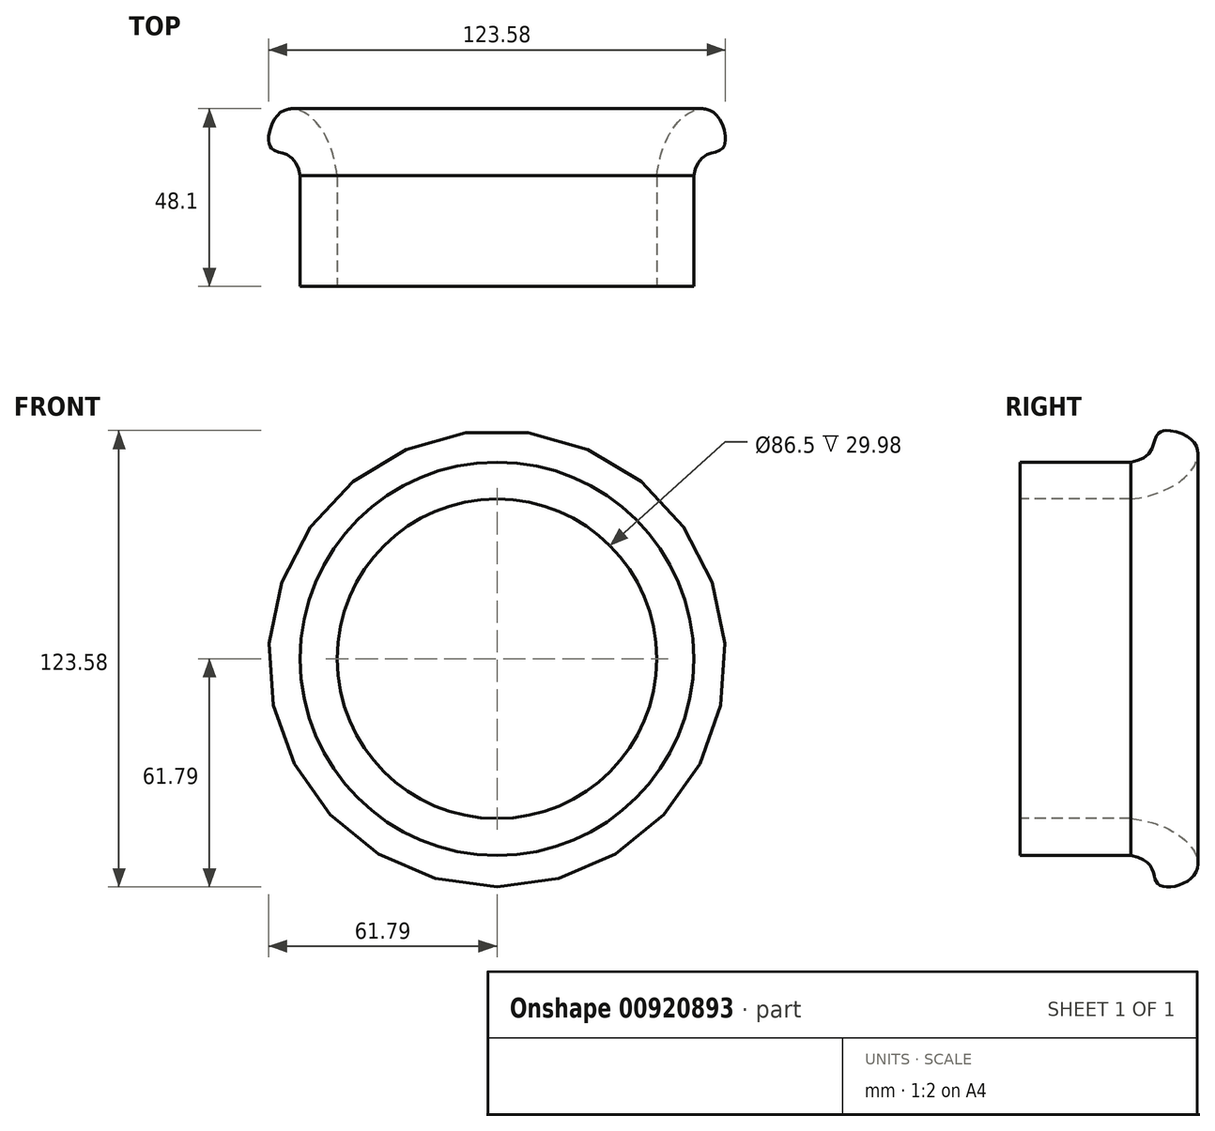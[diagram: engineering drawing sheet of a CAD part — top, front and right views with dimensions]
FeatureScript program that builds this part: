
annotation { "Feature Type Name" : "Feature", "Feature Type Description" : "" }
export const myFeature = defineFeature(function(context is Context, id is Id, definition is map)
    precondition{}
    {
        {
            var Q0;
            Q0=qCreatedBy(makeId("Right.planeOp"),FACE);
            var sketch = newSketch(context, id + "F0", { "sketchPlane" : qUnion([Q0])});
            skLineSegment(sketch, "E0.0", {"start": v(-12.36, -53.25) * mm, "end": v(17.64, -53.25) * mm});
            skFitSpline(sketch, "E1", {"points": [v(17.62, -43.25) * mm, v(35.05, -58.14) * mm, v(25.1, -61.1) * mm, v(17.64, -53.25) * mm], "startDerivative": vector(100.58, -11.6) * mm, "endDerivative": vector(-76.73, 13.48) * mm});
            skLineSegment(sketch, "E2", {"start": v(-12.36, -53.25) * mm, "end": v(-12.36, -43.25) * mm});
            skLineSegment(sketch, "E3", {"start": v(-12.36, -43.25) * mm, "end": v(17.62, -43.25) * mm});
            skSolve(sketch);
        }
        {
            var Q0;
            Q0=qCreatedBy(makeId("Top.planeOp"),FACE);
            var sketch = newSketch(context, id + "F1", { "sketchPlane" : qUnion([Q0])});
            skLineSegment(sketch, "E4", {"start": v(0, 0) * mm, "end": v(0, 75.49) * mm});
            skSolve(sketch);
        }
        {
            var Q0;
            Q0=makeQuery(id+"F0.imprint","IMPRINT",FACE,{"disambiguationData":[TD([[makeQuery(id+"F0.imprint","IMPRINT",EDGE,{"derivedFrom":sQuery(id+"F0.wireOp",EDGE,"E0.0")}),1.0]])]});
            var Q1;
            Q1=sQuery(id+"F1.wireOp",EDGE,"E4");
            revolve(context, id + "F2", {"surfaceOperationType" : NewSurfaceOperationType.NEW, "entities" : qUnion([Q0]), "axis" : qUnion([Q1]), "revolveType" : RevolveType.FULL});
        }
    });
